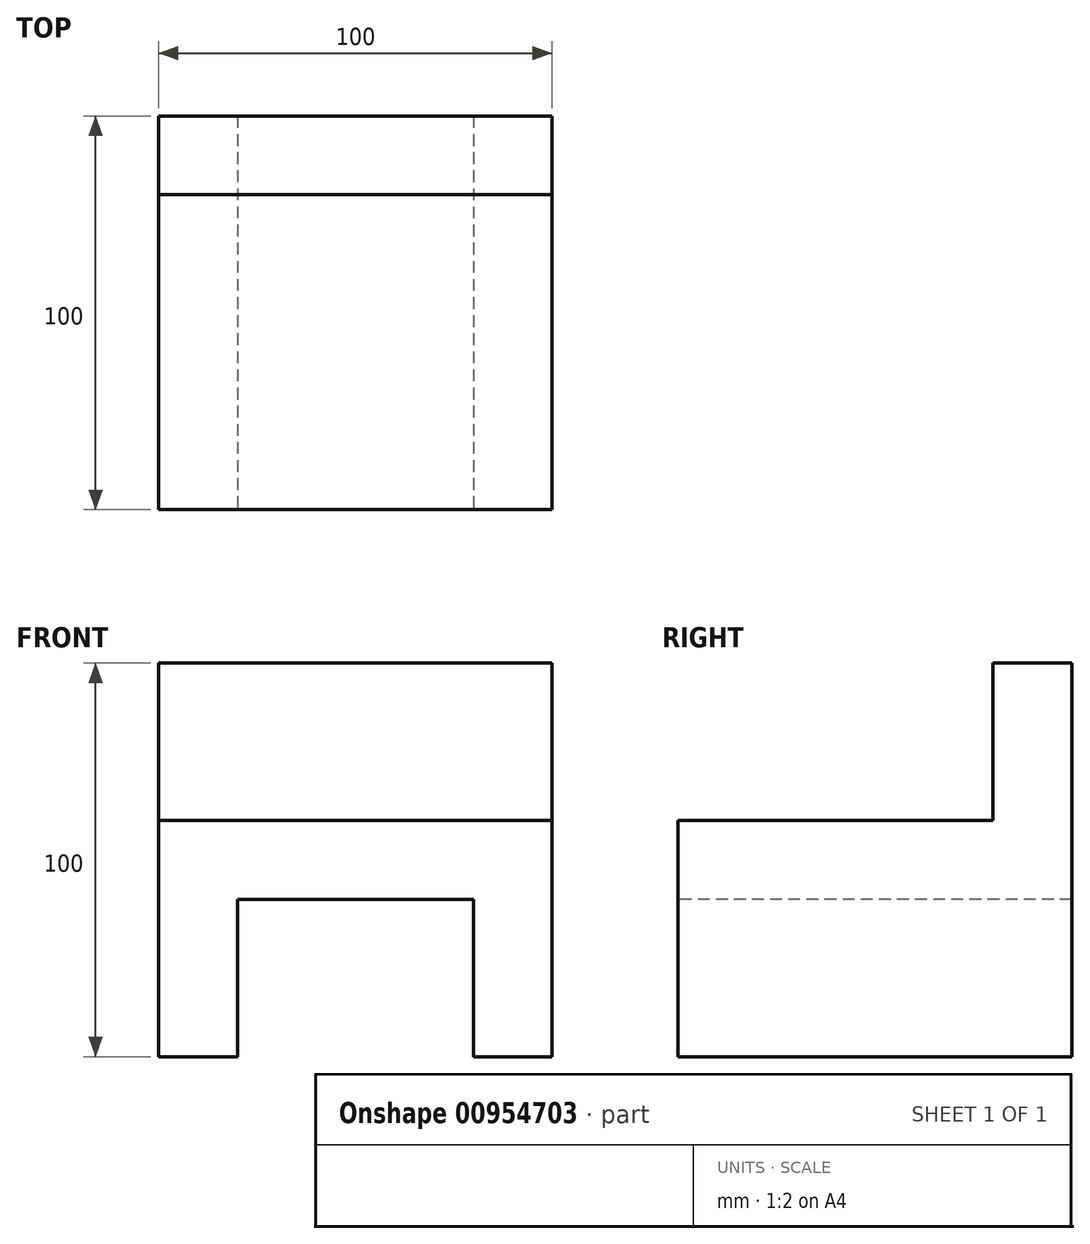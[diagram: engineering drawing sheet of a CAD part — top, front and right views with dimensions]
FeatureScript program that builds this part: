
annotation { "Feature Type Name" : "Feature", "Feature Type Description" : "" }
export const myFeature = defineFeature(function(context is Context, id is Id, definition is map)
    precondition{}
    {
        {
            var Q0;
            Q0=qCreatedBy(makeId("Top.planeOp"),FACE);
            var sketch = newSketch(context, id + "F0", { "sketchPlane" : qUnion([Q0])});
            skLineSegment(sketch, "E0.bottom", {"start": v(50, 50) * mm, "end": v(-50, 50) * mm});
            skLineSegment(sketch, "E0.top", {"start": v(50, -50) * mm, "end": v(-50, -50) * mm});
            skLineSegment(sketch, "E0.left", {"start": v(50, 50) * mm, "end": v(50, -50) * mm});
            skLineSegment(sketch, "E0.right", {"start": v(-50, 50) * mm, "end": v(-50, -50) * mm});
            skPoint(sketch, "E0.middle", {"position": v(0, 0) * mm});
            skSolve(sketch);
        }
        {
            var Q0;
            Q0 = qSketchRegion(id + "F0", true);
            extrude(context, id + "F1", {"entities" : qUnion([Q0]), "depth" : 100 * mm, "offsetDistance" : 25 * mm});
        }
        {
            var Q0;
            Q0=makeQuery(id+"F1.opExtrude","CAP_FACE",FACE,{"disambiguationData":[OSD([sQuery(id+"F0.wireOp",EDGE,"E0.bottom"),sQuery(id+"F0.wireOp",EDGE,"E0.top"),sQuery(id+"F0.wireOp",EDGE,"E0.left"),sQuery(id+"F0.wireOp",EDGE,"E0.right")])],"isStart":false});
            var sketch = newSketch(context, id + "F2", { "sketchPlane" : qUnion([Q0])});
            skLineSegment(sketch, "E1.bottom", {"start": v(-50, -50) * mm, "end": v(50, -50) * mm});
            skLineSegment(sketch, "E1.top", {"start": v(-50, 30) * mm, "end": v(50, 30) * mm});
            skLineSegment(sketch, "E1.left", {"start": v(-50, -50) * mm, "end": v(-50, 30) * mm});
            skLineSegment(sketch, "E1.right", {"start": v(50, -50) * mm, "end": v(50, 30) * mm});
            skSolve(sketch);
        }
        {
            var Q0;
            Q0 = qSketchRegion(id + "F2", true);
            extrude(context, id + "F3", {"entities" : qUnion([Q0]), "operationType" : NewBodyOperationType.REMOVE, "oppositeDirection" : true, "depth" : 40 * mm, "offsetDistance" : 25 * mm});
        }
        {
            var Q0;
            Q0=makeQuery(id+"F1.opExtrude","SWEPT_FACE",FACE,{"disambiguationData":[OSD([sQuery(id+"F0.wireOp",EDGE,"E0.top")])]});
            var sketch = newSketch(context, id + "F4", { "sketchPlane" : qUnion([Q0])});
            skLineSegment(sketch, "E2.bottom", {"start": v(-30, 0) * mm, "end": v(30, 0) * mm});
            skLineSegment(sketch, "E2.top", {"start": v(-30, 40) * mm, "end": v(30, 40) * mm});
            skLineSegment(sketch, "E2.left", {"start": v(-30, 0) * mm, "end": v(-30, 40) * mm});
            skLineSegment(sketch, "E2.right", {"start": v(30, 0) * mm, "end": v(30, 40) * mm});
            skSolve(sketch);
        }
        {
            var Q0;
            Q0=makeQuery(id+"F4.imprint","IMPRINT",FACE,{"disambiguationData":[TD([[makeQuery(id+"F4.imprint","IMPRINT",EDGE,{"derivedFrom":sQuery(id+"F4.wireOp",EDGE,"E2.bottom")}),-1.0]])]});
            extrude(context, id + "F5", {"entities" : qUnion([Q0]), "operationType" : NewBodyOperationType.REMOVE, "endBound" : BoundingType.THROUGH_ALL, "oppositeDirection" : true, "depth" : 25 * mm, "offsetDistance" : 25 * mm});
        }
    });
